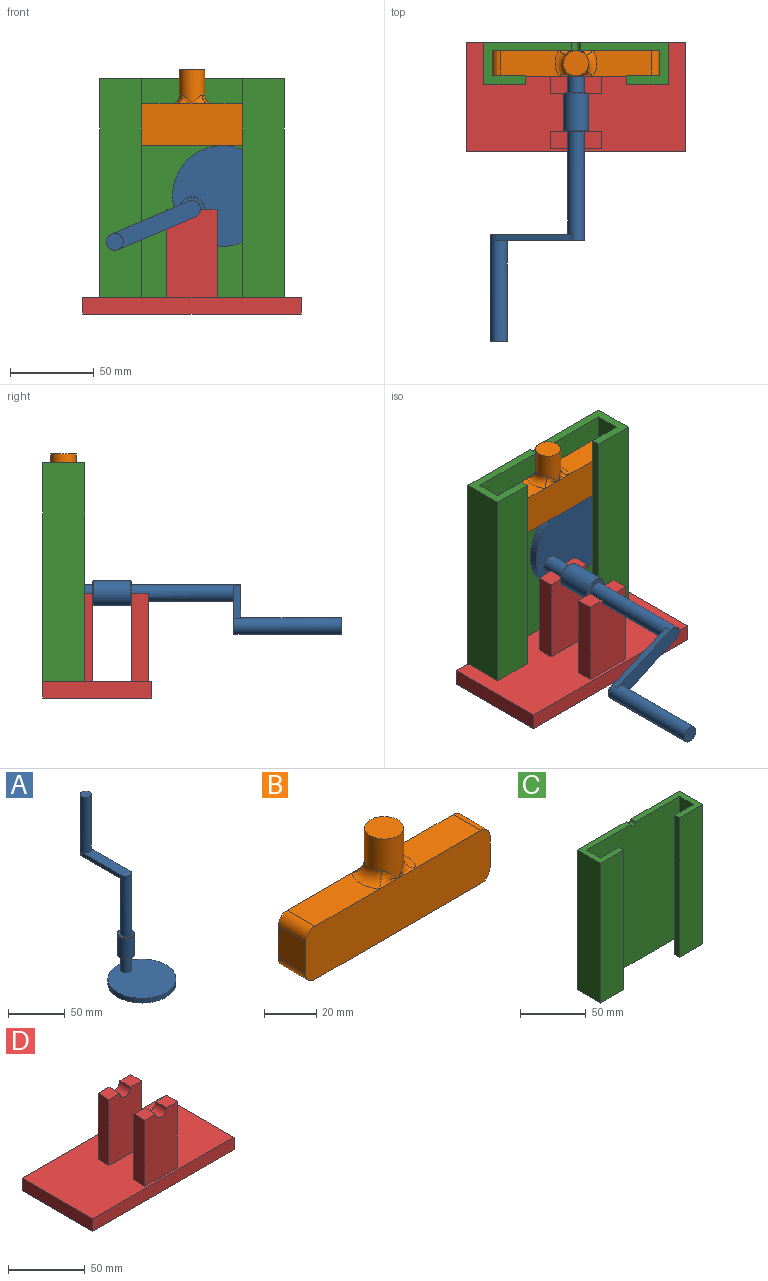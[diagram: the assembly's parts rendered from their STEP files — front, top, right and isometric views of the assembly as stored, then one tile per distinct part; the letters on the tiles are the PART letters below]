
ASSEMBLY  parts=4 mates=3
PART A: 16 faces, bbox 60x105x169 mm
  f0: cylinder r=5mm len=65mm, axis (0,0,-1), area 1979.2mm2, adj f1,f2,f3,f4,f8
  f1: plane 55x10mm, normal (0,0,-1), area 500mm2, adj f0,f2,f3,f5
  f2: plane 50x4mm, normal (1,0,0), area 200mm2, adj f0,f1,f4,f5
  f3: plane 50x4mm, normal (-1,0,0), area 200mm2, adj f0,f1,f4,f5
  f4: plane 55x10mm, normal (0,0,1), area 500mm2, adj f0,f2,f3,f5
  f5: cylinder r=5mm len=64mm, axis (0,0,-1), area 1947.8mm2, adj f1,f2,f3,f4,f6
  f6: plane 10x10mm, normal (0,0,1), area 78.5mm2, adj f5
  f7: cylinder r=7.5mm len=22mm, axis (0,0,-1), area 1036.7mm2, adj f14,f15
  f8: plane 14x14mm, normal (0,0,1), area 75.4mm2, adj f0,f15
  f9: plane 14x14mm, normal (0,0,-1), area 75.4mm2, adj f13,f14
  f10: plane 60x60mm, normal (0,0,-1), area 2827.4mm2, adj f11
  f11: cylinder r=30mm len=60mm, axis (0,0,-1), area 942.5mm2, adj f10,f12
  f12: plane 60x60mm, normal (0,0,1), area 2748.9mm2, adj f11,f13
  f13: cylinder r=5mm len=16mm, axis (0,0,-1), area 502.7mm2, adj f9,f12
  f14: cone r=7.5mm half-angle=45deg, axis (0,0,1), area 32.2mm2, adj f7,f9
  f15: cone r=7mm half-angle=45deg, axis (0,0,-1), area 32.2mm2, adj f7,f8
PART B: 19 faces, bbox 100.7x21.5x45.7 mm
  f0: plane 35x15mm, normal (0,0,1), area 499.5mm2, adj f2,f4,f9,f17
  f1: plane 15x15mm, normal (1,0,0), area 225mm2, adj f2,f4,f8,f10
  f2: plane 100.69x25.69mm, normal (0,1,0), area 2478.5mm2, adj f0,f1,f3,f5,f6,f7,f8,f9
  f3: plane 15x15mm, normal (-1,0,0), area 225mm2, adj f2,f4,f7,f9
  f4: plane 100.69x25.69mm, normal (0,-1,0), area 2478.5mm2, adj f0,f1,f3,f5,f6,f7,f8,f9
  f5: plane 35x15mm, normal (0,0,1), area 499.5mm2, adj f2,f4,f10,f14
  f6: plane 90x15mm, normal (0,0,-1), area 1350mm2, adj f2,f4,f7,f8
  f7: cylinder r=5mm len=15mm, axis (0,-1,0), area 117.8mm2, adj f2,f3,f4,f6
  f8: cylinder r=5mm len=15mm, axis (0,1,0), area 117.8mm2, adj f1,f2,f4,f6
  f9: cylinder r=5mm len=15mm, axis (0,1,0), area 117.8mm2, adj f0,f2,f3,f4
  f10: cylinder r=5mm len=15mm, axis (0,-1,0), area 117.8mm2, adj f1,f2,f4,f5
  f11: cylinder r=7.5mm len=20mm, axis (0,0,-1), area 759.9mm2, adj f12,f13,f14,f15,f16,f17,f18
  f12: plane 15x15mm, normal (0,0,1), area 176.7mm2, adj f11
  f13: bspline ~10.21x5.16mm, area 28.3mm2, adj f4,f11,f14
  f14: torus R=12.5mm, axis (0,0,1), area 94.2mm2, adj f5,f11,f13,f15
  f15: bspline ~10.21x5.16mm, area 28.3mm2, adj f2,f11,f14
  f16: bspline ~10.21x5.16mm, area 28.3mm2, adj f4,f11,f17
  f17: torus R=12.5mm, axis (0,0,1), area 94.2mm2, adj f0,f11,f16,f18
  f18: bspline ~10.21x5.16mm, area 28.3mm2, adj f2,f11,f17
PART C: 16 faces, bbox 110x25x130 mm
  f0: plane 52.5x25mm, normal (0,0,1), area 462.5mm2, adj f2,f4,f5,f6,f7,f8,f14,f15
  f1: plane 52.5x25mm, normal (0,0,1), area 462.5mm2, adj f2,f4,f5,f9,f10,f11,f12,f13
  f2: plane 130x100mm, normal (0,-1,0), area 12990.2mm2, adj f0,f1,f3,f5,f8,f9
  f3: plane 110x25mm, normal (0,0,-1), area 950mm2, adj f2,f4,f6,f7,f8,f9,f10,f11
  f4: plane 130x110mm, normal (0,1,0), area 14290.2mm2, adj f0,f1,f3,f5,f7,f11
  f5: cylinder r=2.5mm len=5mm, axis (0,-1,0), area 39.3mm2, adj f0,f1,f2,f4
  f6: plane 130x25mm, normal (0,-1,0), area 3250mm2, adj f0,f3,f7,f15
  f7: plane 130x25mm, normal (-1,0,0), area 3250mm2, adj f0,f3,f4,f6
  f8: plane 130x15mm, normal (1,0,0), area 1950mm2, adj f0,f2,f3,f14
  f9: plane 130x15mm, normal (-1,0,0), area 1950mm2, adj f1,f2,f3,f12
  f10: plane 130x25mm, normal (0,-1,0), area 3250mm2, adj f1,f3,f11,f13
  f11: plane 130x25mm, normal (1,0,0), area 3250mm2, adj f1,f3,f4,f10
  f12: plane 130x20mm, normal (0,1,0), area 2600mm2, adj f1,f3,f9,f13
  f13: plane 130x5mm, normal (-1,0,0), area 650mm2, adj f1,f3,f10,f12
  f14: plane 130x20mm, normal (0,1,0), area 2600mm2, adj f0,f3,f8,f15
  f15: plane 130x5mm, normal (1,0,0), area 650mm2, adj f0,f3,f6,f14
PART D: 20 faces, bbox 130x65x62.5 mm
  f0: plane 52.5x30mm, normal (0,-1,0), area 1535.7mm2, adj f1,f2,f5,f11,f13,f19
  f1: plane 10x10mm, normal (0,0,1), area 100mm2, adj f0,f12,f13,f19
  f2: plane 10x10mm, normal (0,0,1), area 100mm2, adj f0,f11,f12,f19
  f3: plane 10x10mm, normal (0,0,1), area 100mm2, adj f14,f16,f17,f18
  f4: plane 10x10mm, normal (0,0,1), area 100mm2, adj f14,f15,f16,f18
  f5: plane 130x65mm, normal (0,0,1), area 7850mm2, adj f0,f6,f7,f8,f9,f11,f12,f13
  f6: plane 130x10mm, normal (0,-1,0), area 1300mm2, adj f5,f7,f9,f10
  f7: plane 65x10mm, normal (1,0,0), area 650mm2, adj f5,f6,f8,f10
  f8: plane 130x10mm, normal (0,1,0), area 1300mm2, adj f5,f7,f9,f10
  f9: plane 65x10mm, normal (-1,0,0), area 650mm2, adj f5,f6,f8,f10
  f10: plane 130x65mm, normal (0,0,-1), area 8450mm2, adj f6,f7,f8,f9
  f11: plane 52.5x10mm, normal (1,0,0), area 525mm2, adj f0,f2,f5,f12
  f12: plane 52.5x30mm, normal (0,1,0), area 1535.7mm2, adj f1,f2,f5,f11,f13,f19
  f13: plane 52.5x10mm, normal (-1,0,0), area 525mm2, adj f0,f1,f5,f12
  f14: plane 52.5x30mm, normal (0,-1,0), area 1535.7mm2, adj f3,f4,f5,f15,f17,f18
  f15: plane 52.5x10mm, normal (1,0,0), area 525mm2, adj f4,f5,f14,f16
  f16: plane 52.5x30mm, normal (0,1,0), area 1535.7mm2, adj f3,f4,f5,f15,f17,f18
  f17: plane 52.5x10mm, normal (-1,0,0), area 525mm2, adj f3,f5,f14,f16
  f18: cylinder r=5mm len=10mm, axis (0,-1,0), area 157.1mm2, adj f3,f4,f14,f16
  f19: cylinder r=5mm len=10mm, axis (0,-1,0), area 157.1mm2, adj f0,f1,f2,f12
PLACE A rot(axis=(0.42,-0.64,0.64),134.1deg) t=(18.4,23.5,70.33)mm
PLACE B t=(0,20,100.33)mm
PLACE C t=(41.68,32.5,91.41)mm
PLACE D at identity fixed
MATE slider B.f11 <-> C.f3  axis (0,0,1) through (0,20,100.33)mm
MATE fastened C.f3 <-> D.f5  axis (0,0,1) through (0,32.5,10)mm
MATE revolute D.f18 <-> A.f0  axis (0,-1,0) through (0,-30.5,62.5)mm
